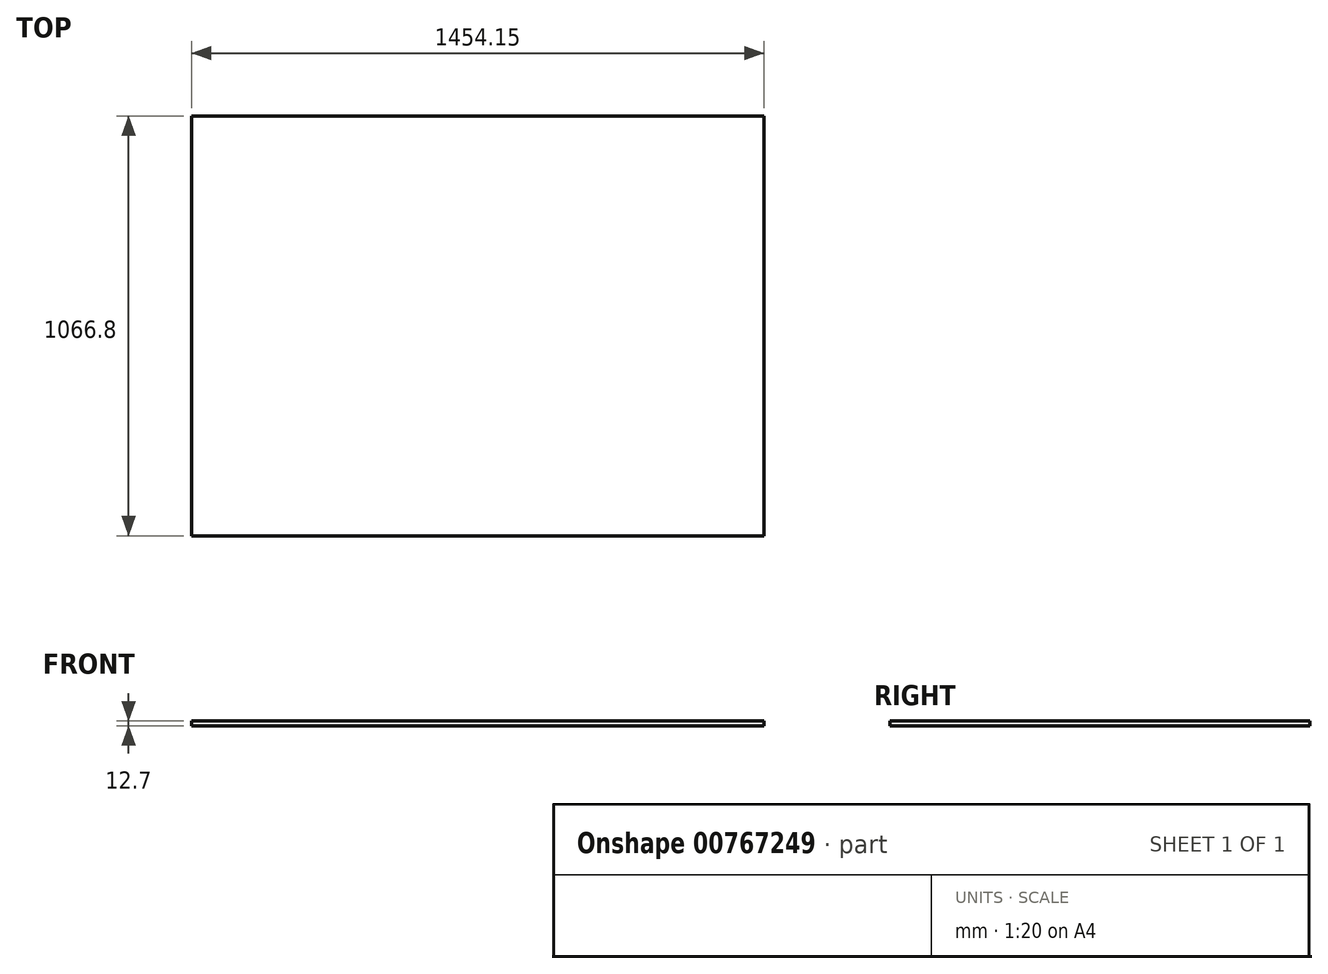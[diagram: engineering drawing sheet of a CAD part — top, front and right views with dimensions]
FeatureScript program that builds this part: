
annotation { "Feature Type Name" : "Feature", "Feature Type Description" : "" }
export const myFeature = defineFeature(function(context is Context, id is Id, definition is map)
    precondition{}
    {
        {
            var Q0;
            Q0=qCreatedBy(makeId("Top.planeOp"),FACE);
            var sketch = newSketch(context, id + "F0", { "sketchPlane" : qUnion([Q0])});
            skLineSegment(sketch, "E0.bottom", {"start": v(-725.7, 631.62) * mm, "end": v(728.45, 631.62) * mm});
            skLineSegment(sketch, "E0.top", {"start": v(-725.7, -435.18) * mm, "end": v(728.45, -435.18) * mm});
            skLineSegment(sketch, "E0.left", {"start": v(-725.7, 631.62) * mm, "end": v(-725.7, -435.18) * mm});
            skLineSegment(sketch, "E0.right", {"start": v(728.45, 631.62) * mm, "end": v(728.45, -435.18) * mm});
            skLineSegment(sketch, "E1.top", {"start": v(-725.7, -358.98) * mm, "end": v(728.45, -358.98) * mm});
            skLineSegment(sketch, "E1.left", {"start": v(-725.7, -435.18) * mm, "end": v(-725.7, -358.98) * mm});
            skLineSegment(sketch, "E1.right", {"start": v(728.45, -435.18) * mm, "end": v(728.45, -358.98) * mm});
            skLineSegment(sketch, "E2.bottom", {"start": v(728.45, -435.18) * mm, "end": v(652.25, -435.18) * mm});
            skLineSegment(sketch, "E2.top", {"start": v(728.45, 631.62) * mm, "end": v(652.25, 631.62) * mm});
            skLineSegment(sketch, "E2.left", {"start": v(728.45, -435.18) * mm, "end": v(728.45, 631.62) * mm});
            skLineSegment(sketch, "E2.right", {"start": v(652.25, -435.18) * mm, "end": v(652.25, 631.62) * mm});
            skLineSegment(sketch, "E3.top", {"start": v(-725.7, 555.42) * mm, "end": v(728.45, 555.42) * mm});
            skLineSegment(sketch, "E3.left", {"start": v(-725.7, 631.62) * mm, "end": v(-725.7, 555.42) * mm});
            skLineSegment(sketch, "E3.right", {"start": v(728.45, 631.62) * mm, "end": v(728.45, 555.42) * mm});
            skLineSegment(sketch, "E4.bottom", {"start": v(-725.7, -435.18) * mm, "end": v(-649.5, -435.18) * mm});
            skLineSegment(sketch, "E4.top", {"start": v(-725.7, 631.62) * mm, "end": v(-649.5, 631.62) * mm});
            skLineSegment(sketch, "E4.left", {"start": v(-725.7, -435.18) * mm, "end": v(-725.7, 631.62) * mm});
            skLineSegment(sketch, "E4.right", {"start": v(-649.5, -435.18) * mm, "end": v(-649.5, 631.62) * mm});
            skLineSegment(sketch, "E5.bottom", {"start": v(-649.5, 555.42) * mm, "end": v(-389.15, 555.42) * mm});
            skLineSegment(sketch, "E5.top", {"start": v(-649.5, -358.98) * mm, "end": v(-389.15, -358.98) * mm});
            skLineSegment(sketch, "E5.left", {"start": v(-649.5, 555.42) * mm, "end": v(-649.5, -358.98) * mm});
            skLineSegment(sketch, "E5.right", {"start": v(-389.15, 555.42) * mm, "end": v(-389.15, -358.98) * mm});
            skLineSegment(sketch, "E6.bottom", {"start": v(-389.15, 555.42) * mm, "end": v(-128.8, 555.42) * mm});
            skLineSegment(sketch, "E6.top", {"start": v(-389.15, -358.98) * mm, "end": v(-128.8, -358.98) * mm});
            skLineSegment(sketch, "E6.right", {"start": v(-128.8, 555.42) * mm, "end": v(-128.8, -358.98) * mm});
            skLineSegment(sketch, "E7.bottom", {"start": v(-128.8, 555.42) * mm, "end": v(131.55, 555.42) * mm});
            skLineSegment(sketch, "E7.top", {"start": v(-128.8, -358.98) * mm, "end": v(131.55, -358.98) * mm});
            skLineSegment(sketch, "E7.right", {"start": v(131.55, 555.42) * mm, "end": v(131.55, -358.98) * mm});
            skLineSegment(sketch, "E8.bottom", {"start": v(131.55, 555.42) * mm, "end": v(391.9, 555.42) * mm});
            skLineSegment(sketch, "E8.top", {"start": v(131.55, -358.98) * mm, "end": v(391.9, -358.98) * mm});
            skLineSegment(sketch, "E8.right", {"start": v(391.9, 555.42) * mm, "end": v(391.9, -358.98) * mm});
            skLineSegment(sketch, "E9.bottom", {"start": v(-649.5, 555.42) * mm, "end": v(652.25, 555.42) * mm});
            skLineSegment(sketch, "E9.top", {"start": v(-649.5, 326.82) * mm, "end": v(652.25, 326.82) * mm});
            skLineSegment(sketch, "E9.left", {"start": v(-649.5, 555.42) * mm, "end": v(-649.5, 326.82) * mm});
            skLineSegment(sketch, "E9.right", {"start": v(652.25, 555.42) * mm, "end": v(652.25, 326.82) * mm});
            skLineSegment(sketch, "E10.top", {"start": v(-649.5, 98.22) * mm, "end": v(652.25, 98.22) * mm});
            skLineSegment(sketch, "E10.left", {"start": v(-649.5, 326.82) * mm, "end": v(-649.5, 98.22) * mm});
            skLineSegment(sketch, "E10.right", {"start": v(652.25, 326.82) * mm, "end": v(652.25, 98.22) * mm});
            skLineSegment(sketch, "E11.top", {"start": v(-649.5, -130.38) * mm, "end": v(652.25, -130.38) * mm});
            skLineSegment(sketch, "E11.left", {"start": v(-649.5, 98.22) * mm, "end": v(-649.5, -130.38) * mm});
            skLineSegment(sketch, "E11.right", {"start": v(652.25, 98.22) * mm, "end": v(652.25, -130.38) * mm});
            skSolve(sketch);
        }
        {
            var Q0;
            {var subQ0=sQuery(id+"F0.wireOp",EDGE,"E4.right");var subQ1=sQuery(id+"F0.wireOp",EDGE,"E0.bottom");var subQ2=makeQuery(id+"F0.imprint","INTERSECT",VERTEX,{"derivedFrom":[subQ1,subQ0]});Q0=makeQuery(id+"F0.imprint","IMPRINT",FACE,{"disambiguationData":[TD([[makeQuery(id+"F0.imprint","IMPRINT",EDGE,{"disambiguationData":[TD([[subQ2,1.0]])],"derivedFrom":subQ1}),-1.0]])]});}
            var Q1;
            {var subQ4=sQuery(id+"F0.wireOp",EDGE,"E0.bottom");var subQ7=sQuery(id+"F0.wireOp",EDGE,"E4.right");var subQ9=makeQuery(id+"F0.imprint","INTERSECT",VERTEX,{"derivedFrom":[subQ4,subQ7]});Q1=makeQuery(id+"F0.imprint","IMPRINT",FACE,{"disambiguationData":[TD([[makeQuery(id+"F0.imprint","IMPRINT",EDGE,{"disambiguationData":[TD([[subQ9,-1.0]])],"derivedFrom":subQ4}),-1.0]])]});}
            var Q2;
            {var subQ0=sQuery(id+"F0.wireOp",EDGE,"E4.right");var subQ1=sQuery(id+"F0.wireOp",EDGE,"E3.top");var subQ2=makeQuery(id+"F0.imprint","INTERSECT",VERTEX,{"derivedFrom":[subQ1,subQ0]});Q2=makeQuery(id+"F0.imprint","IMPRINT",FACE,{"disambiguationData":[TD([[makeQuery(id+"F0.imprint","IMPRINT",EDGE,{"disambiguationData":[TD([[subQ2,-1.0]])],"derivedFrom":subQ1}),-1.0]])]});}
            var Q3;
            {var subQ4=sQuery(id+"F0.wireOp",EDGE,"E0.left");var subQ6=sQuery(id+"F0.wireOp",EDGE,"E3.top");var subQ7=makeQuery(id+"F0.imprint","INTERSECT",VERTEX,{"derivedFrom":[subQ4,subQ6]});Q3=makeQuery(id+"F0.imprint","IMPRINT",FACE,{"disambiguationData":[TD([[makeQuery(id+"F0.imprint","IMPRINT",EDGE,{"disambiguationData":[TD([[subQ7,-1.0]])],"derivedFrom":subQ4}),1.0]])]});}
            var Q4;
            {var subQ0=sQuery(id+"F0.wireOp",EDGE,"E4.right");var subQ1=sQuery(id+"F0.wireOp",EDGE,"E0.top");var subQ2=makeQuery(id+"F0.imprint","INTERSECT",VERTEX,{"derivedFrom":[subQ1,subQ0]});Q4=makeQuery(id+"F0.imprint","IMPRINT",FACE,{"disambiguationData":[TD([[makeQuery(id+"F0.imprint","IMPRINT",EDGE,{"disambiguationData":[TD([[subQ2,1.0]])],"derivedFrom":subQ1}),1.0]])]});}
            var Q5;
            {var subQ3=sQuery(id+"F0.wireOp",EDGE,"E4.right");var subQ4=sQuery(id+"F0.wireOp",EDGE,"E0.top");var subQ5=makeQuery(id+"F0.imprint","INTERSECT",VERTEX,{"derivedFrom":[subQ4,subQ3]});Q5=makeQuery(id+"F0.imprint","IMPRINT",FACE,{"disambiguationData":[TD([[makeQuery(id+"F0.imprint","IMPRINT",EDGE,{"disambiguationData":[TD([[subQ5,-1.0]])],"derivedFrom":subQ4}),1.0]])]});}
            var Q6;
            {var subQ3=sQuery(id+"F0.wireOp",EDGE,"E3.top");var subQ4=sQuery(id+"F0.wireOp",EDGE,"E0.right");var subQ5=makeQuery(id+"F0.imprint","INTERSECT",VERTEX,{"derivedFrom":[subQ4,subQ3]});Q6=makeQuery(id+"F0.imprint","IMPRINT",FACE,{"disambiguationData":[TD([[makeQuery(id+"F0.imprint","IMPRINT",EDGE,{"disambiguationData":[TD([[subQ5,-1.0]])],"derivedFrom":subQ4}),-1.0]])]});}
            var Q7;
            {var subQ0=sQuery(id+"F0.wireOp",EDGE,"E0.right");var subQ1=sQuery(id+"F0.wireOp",EDGE,"E0.top");var subQ2=makeQuery(id+"F0.imprint","INTERSECT",VERTEX,{"derivedFrom":[subQ1,subQ0]});Q7=makeQuery(id+"F0.imprint","IMPRINT",FACE,{"disambiguationData":[TD([[makeQuery(id+"F0.imprint","IMPRINT",EDGE,{"disambiguationData":[TD([[subQ2,1.0]])],"derivedFrom":subQ1}),1.0]])]});}
            var Q8;
            {var subQ0=sQuery(id+"F0.wireOp",EDGE,"E2.right");var subQ1=sQuery(id+"F0.wireOp",EDGE,"E0.bottom");var subQ2=makeQuery(id+"F0.imprint","INTERSECT",VERTEX,{"derivedFrom":[subQ1,subQ0]});Q8=makeQuery(id+"F0.imprint","IMPRINT",FACE,{"disambiguationData":[TD([[makeQuery(id+"F0.imprint","IMPRINT",EDGE,{"disambiguationData":[TD([[subQ2,-1.0]])],"derivedFrom":subQ1}),-1.0]])]});}
            var Q9;
            {var subQ0=sQuery(id+"F0.wireOp",EDGE,"E5.right");var subQ1=sQuery(id+"F0.wireOp",EDGE,"E3.top");var subQ2=makeQuery(id+"F0.imprint","INTERSECT",VERTEX,{"derivedFrom":[subQ1,subQ0]});Q9=makeQuery(id+"F0.imprint","IMPRINT",FACE,{"disambiguationData":[TD([[makeQuery(id+"F0.imprint","IMPRINT",EDGE,{"disambiguationData":[TD([[subQ2,-1.0]])],"derivedFrom":subQ1}),-1.0]])]});}
            var Q10;
            {var subQ0=sQuery(id+"F0.wireOp",EDGE,"E6.right");var subQ1=sQuery(id+"F0.wireOp",EDGE,"E3.top");var subQ2=makeQuery(id+"F0.imprint","INTERSECT",VERTEX,{"derivedFrom":[subQ1,subQ0]});Q10=makeQuery(id+"F0.imprint","IMPRINT",FACE,{"disambiguationData":[TD([[makeQuery(id+"F0.imprint","IMPRINT",EDGE,{"disambiguationData":[TD([[subQ2,-1.0]])],"derivedFrom":subQ1}),-1.0]])]});}
            var Q11;
            {var subQ0=sQuery(id+"F0.wireOp",EDGE,"E8.right");var subQ1=sQuery(id+"F0.wireOp",EDGE,"E3.top");var subQ2=makeQuery(id+"F0.imprint","INTERSECT",VERTEX,{"derivedFrom":[subQ1,subQ0]});Q11=makeQuery(id+"F0.imprint","IMPRINT",FACE,{"disambiguationData":[TD([[makeQuery(id+"F0.imprint","IMPRINT",EDGE,{"disambiguationData":[TD([[subQ2,1.0]])],"derivedFrom":subQ1}),-1.0]])]});}
            var Q12;
            {var subQ0=sQuery(id+"F0.wireOp",EDGE,"E9.top");var subQ1=sQuery(id+"F0.wireOp",EDGE,"E2.right");var subQ2=makeQuery(id+"F0.imprint","INTERSECT",VERTEX,{"derivedFrom":[subQ1,subQ0]});Q12=makeQuery(id+"F0.imprint","IMPRINT",FACE,{"disambiguationData":[TD([[makeQuery(id+"F0.imprint","IMPRINT",EDGE,{"disambiguationData":[TD([[subQ2,-1.0]])],"derivedFrom":subQ1}),1.0]])]});}
            var Q13;
            {var subQ0=sQuery(id+"F0.wireOp",EDGE,"E9.top");var subQ1=sQuery(id+"F0.wireOp",EDGE,"E2.right");var subQ2=makeQuery(id+"F0.imprint","INTERSECT",VERTEX,{"derivedFrom":[subQ1,subQ0]});Q13=makeQuery(id+"F0.imprint","IMPRINT",FACE,{"disambiguationData":[TD([[makeQuery(id+"F0.imprint","IMPRINT",EDGE,{"disambiguationData":[TD([[subQ2,1.0]])],"derivedFrom":subQ1}),1.0]])]});}
            var Q14;
            {var subQ0=sQuery(id+"F0.wireOp",EDGE,"E9.top");var subQ1=sQuery(id+"F0.wireOp",EDGE,"E7.right");var subQ2=makeQuery(id+"F0.imprint","INTERSECT",VERTEX,{"derivedFrom":[subQ1,subQ0]});Q14=makeQuery(id+"F0.imprint","IMPRINT",FACE,{"disambiguationData":[TD([[makeQuery(id+"F0.imprint","IMPRINT",EDGE,{"disambiguationData":[TD([[subQ2,-1.0]])],"derivedFrom":subQ1}),1.0]])]});}
            var Q15;
            {var subQ0=sQuery(id+"F0.wireOp",EDGE,"E9.top");var subQ1=sQuery(id+"F0.wireOp",EDGE,"E6.right");var subQ2=makeQuery(id+"F0.imprint","INTERSECT",VERTEX,{"derivedFrom":[subQ1,subQ0]});Q15=makeQuery(id+"F0.imprint","IMPRINT",FACE,{"disambiguationData":[TD([[makeQuery(id+"F0.imprint","IMPRINT",EDGE,{"disambiguationData":[TD([[subQ2,-1.0]])],"derivedFrom":subQ1}),1.0]])]});}
            var Q16;
            {var subQ0=sQuery(id+"F0.wireOp",EDGE,"E9.top");var subQ1=sQuery(id+"F0.wireOp",EDGE,"E5.right");var subQ2=makeQuery(id+"F0.imprint","INTERSECT",VERTEX,{"derivedFrom":[subQ1,subQ0]});Q16=makeQuery(id+"F0.imprint","IMPRINT",FACE,{"disambiguationData":[TD([[makeQuery(id+"F0.imprint","IMPRINT",EDGE,{"disambiguationData":[TD([[subQ2,-1.0]])],"derivedFrom":subQ1}),1.0]])]});}
            var Q17;
            {var subQ0=sQuery(id+"F0.wireOp",EDGE,"E10.top");var subQ1=sQuery(id+"F0.wireOp",EDGE,"E4.right");var subQ2=makeQuery(id+"F0.imprint","INTERSECT",VERTEX,{"derivedFrom":[subQ1,subQ0]});Q17=makeQuery(id+"F0.imprint","IMPRINT",FACE,{"disambiguationData":[TD([[makeQuery(id+"F0.imprint","IMPRINT",EDGE,{"disambiguationData":[TD([[subQ2,-1.0]])],"derivedFrom":subQ1}),-1.0]])]});}
            var Q18;
            {var subQ0=sQuery(id+"F0.wireOp",EDGE,"E10.top");var subQ1=sQuery(id+"F0.wireOp",EDGE,"E4.right");var subQ2=makeQuery(id+"F0.imprint","INTERSECT",VERTEX,{"derivedFrom":[subQ1,subQ0]});Q18=makeQuery(id+"F0.imprint","IMPRINT",FACE,{"disambiguationData":[TD([[makeQuery(id+"F0.imprint","IMPRINT",EDGE,{"disambiguationData":[TD([[subQ2,1.0]])],"derivedFrom":subQ1}),-1.0]])]});}
            var Q19;
            {var subQ0=sQuery(id+"F0.wireOp",EDGE,"E11.top");var subQ1=sQuery(id+"F0.wireOp",EDGE,"E5.right");var subQ2=makeQuery(id+"F0.imprint","INTERSECT",VERTEX,{"derivedFrom":[subQ1,subQ0]});Q19=makeQuery(id+"F0.imprint","IMPRINT",FACE,{"disambiguationData":[TD([[makeQuery(id+"F0.imprint","IMPRINT",EDGE,{"disambiguationData":[TD([[subQ2,1.0]])],"derivedFrom":subQ1}),1.0]])]});}
            var Q20;
            {var subQ0=sQuery(id+"F0.wireOp",EDGE,"E11.top");var subQ1=sQuery(id+"F0.wireOp",EDGE,"E6.right");var subQ2=makeQuery(id+"F0.imprint","INTERSECT",VERTEX,{"derivedFrom":[subQ1,subQ0]});Q20=makeQuery(id+"F0.imprint","IMPRINT",FACE,{"disambiguationData":[TD([[makeQuery(id+"F0.imprint","IMPRINT",EDGE,{"disambiguationData":[TD([[subQ2,1.0]])],"derivedFrom":subQ1}),1.0]])]});}
            var Q21;
            {var subQ0=sQuery(id+"F0.wireOp",EDGE,"E11.top");var subQ1=sQuery(id+"F0.wireOp",EDGE,"E7.right");var subQ2=makeQuery(id+"F0.imprint","INTERSECT",VERTEX,{"derivedFrom":[subQ1,subQ0]});Q21=makeQuery(id+"F0.imprint","IMPRINT",FACE,{"disambiguationData":[TD([[makeQuery(id+"F0.imprint","IMPRINT",EDGE,{"disambiguationData":[TD([[subQ2,1.0]])],"derivedFrom":subQ1}),1.0]])]});}
            var Q22;
            {var subQ0=sQuery(id+"F0.wireOp",EDGE,"E10.top");var subQ1=sQuery(id+"F0.wireOp",EDGE,"E2.right");var subQ2=makeQuery(id+"F0.imprint","INTERSECT",VERTEX,{"derivedFrom":[subQ1,subQ0]});Q22=makeQuery(id+"F0.imprint","IMPRINT",FACE,{"disambiguationData":[TD([[makeQuery(id+"F0.imprint","IMPRINT",EDGE,{"disambiguationData":[TD([[subQ2,1.0]])],"derivedFrom":subQ1}),1.0]])]});}
            var Q23;
            {var subQ0=sQuery(id+"F0.wireOp",EDGE,"E2.right");var subQ1=sQuery(id+"F0.wireOp",EDGE,"E1.top");var subQ2=makeQuery(id+"F0.imprint","INTERSECT",VERTEX,{"derivedFrom":[subQ1,subQ0]});Q23=makeQuery(id+"F0.imprint","IMPRINT",FACE,{"disambiguationData":[TD([[makeQuery(id+"F0.imprint","IMPRINT",EDGE,{"disambiguationData":[TD([[subQ2,1.0]])],"derivedFrom":subQ1}),1.0]])]});}
            var Q24;
            {var subQ0=sQuery(id+"F0.wireOp",EDGE,"E7.right");var subQ1=sQuery(id+"F0.wireOp",EDGE,"E1.top");var subQ2=makeQuery(id+"F0.imprint","INTERSECT",VERTEX,{"derivedFrom":[subQ1,subQ0]});Q24=makeQuery(id+"F0.imprint","IMPRINT",FACE,{"disambiguationData":[TD([[makeQuery(id+"F0.imprint","IMPRINT",EDGE,{"disambiguationData":[TD([[subQ2,-1.0]])],"derivedFrom":subQ1}),1.0]])]});}
            var Q25;
            {var subQ0=sQuery(id+"F0.wireOp",EDGE,"E7.right");var subQ1=sQuery(id+"F0.wireOp",EDGE,"E1.top");var subQ2=makeQuery(id+"F0.imprint","INTERSECT",VERTEX,{"derivedFrom":[subQ1,subQ0]});Q25=makeQuery(id+"F0.imprint","IMPRINT",FACE,{"disambiguationData":[TD([[makeQuery(id+"F0.imprint","IMPRINT",EDGE,{"disambiguationData":[TD([[subQ2,1.0]])],"derivedFrom":subQ1}),1.0]])]});}
            var Q26;
            {var subQ0=sQuery(id+"F0.wireOp",EDGE,"E6.right");var subQ1=sQuery(id+"F0.wireOp",EDGE,"E1.top");var subQ2=makeQuery(id+"F0.imprint","INTERSECT",VERTEX,{"derivedFrom":[subQ1,subQ0]});Q26=makeQuery(id+"F0.imprint","IMPRINT",FACE,{"disambiguationData":[TD([[makeQuery(id+"F0.imprint","IMPRINT",EDGE,{"disambiguationData":[TD([[subQ2,1.0]])],"derivedFrom":subQ1}),1.0]])]});}
            var Q27;
            {var subQ0=sQuery(id+"F0.wireOp",EDGE,"E4.right");var subQ1=sQuery(id+"F0.wireOp",EDGE,"E1.top");var subQ2=makeQuery(id+"F0.imprint","INTERSECT",VERTEX,{"derivedFrom":[subQ1,subQ0]});Q27=makeQuery(id+"F0.imprint","IMPRINT",FACE,{"disambiguationData":[TD([[makeQuery(id+"F0.imprint","IMPRINT",EDGE,{"disambiguationData":[TD([[subQ2,-1.0]])],"derivedFrom":subQ1}),1.0]])]});}
            extrude(context, id + "F1", {"entities" : qUnion([Q0, Q1, Q2, Q3, Q4, Q5, Q6, Q7, Q8, Q9, Q10, Q11, Q12, Q13, Q14, Q15, Q16, Q17, Q18, Q19, Q20, Q21, Q22, Q23, Q24, Q25, Q26, Q27]), "depth" : 12.7 * mm, "offsetDistance" : 25.4 * mm});
        }
    });
